# Revit family: Domotics-DomoticSolutions-GEWISS-BUS-KNX_TEMPERATURE_SENSOR
name_source: partatom
category: Apparecchi elettrici
revit_build: Autodesk Revit 2016 (Build: 20161004_0715(x64)
units: mm (PartAtom-declared; Revit-internal decimal feet)

## family parameters
Condiviso = No
Host = Superficie
Mantenere orientamento annotazione = Sì
Punto di calcolo locali = No
Quota connettore circolare = Usa diametro
Taglio con vuoti quando caricato = Sì
Tipo di parte = Normale

## types (18) — shared parameters
Catalogue = DOMOTICS
Catalogue Range = H&B AUTOMATION
IDF = 93389465-b77d-4902-bf96-7a1d22c4ea34
IDT = eb8a331f-fb03-4651-b93d-be283b5d4bed
Immagine tipo = GW14900.jpg
Larghezza sonda = 23 mm  [stored 0.0754593 ft]
No. Chorus modules = 1
No. Chorus modules: = 1
Produttore = GEWISS S.p.A.
Prospetto di default = 1219 mm
SEO = Sensor
Simbolo = SIMBOLO TERMOSTATO : KNX
Technical sheet = https://www.gewiss.com
Tipo = BUS KNX SONDE TERMOREGOLAZIONE_BASE : GW14900 - Titanio
URL = https://www.gewiss.com
Version file RFA = 18.0

## per-type parameters (varying)
| type | Colour | Descrizione | EAN code | Electrocod | Humidity sensor | Modello | Technology | Type |
| GW12799 - Black | Black | KNX TEMPERATURE SENSOR 1M BLACK | 8011564785021 | 3841 |  | GW12799 | KNX | KNX |
| GW12762H - Black - Easy | Black | KNX/EASY HUM./TEMP.SENSORS BLACK | 8011564821989 | 1434 | Built-in | GW12762H |  | KNX |
| GW10762H - White - Easy | White | KNX/EASY HUM./TEMP.SENSORS WHITE | 8011564821972 | 1434 | Built-in | GW10762H |  | KNX |
| GW12900 - Black | Black | F.M.TEMPERATURE SENSOR BLACK | 8011564821927 | 1434 |  | GW12900 |  |  |
| GW10900 - White | White | F.M.TEMPERATURE SENSOR WHITE | 8011564821910 | 1434 |  | GW10900 |  |  |
| GW12769H - Black | Black | EASY HUMIDITY/TEMPERATURE SENSORS BLACK | 8011564809130 | 3841 | Built-in | GW12769H | KNX Easy | KNX Easy |
| GW10799H - White | White | KNX HUMIDITY/TEMPERATURE SENSORS WHITE | 8011564809123 | 3841 | Built-in | GW10799H | KNX | KNX |
| GW14769 - Titanium - Easy | Titanium | EASY TEMPERATURE SENSOR 1M TITANIUM | 8011564785120 | 0144 |  | GW14769 | KNX Easy | KNX Easy |
| GW12799H - Black | Black | KNX HUMIDITY/TEMPERATURE SENSORS BLACK | 8011564809147 | 3841 | Built-in | GW12799H | KNX | KNX |
| GW10799 - White | White | KNX TEMPERATURE SENSOR 1M WHITE | 8011564785014 | 3841 |  | GW10799 | KNX | KNX |
| GW10769 - White - Easy | White | EASY TEMPERATURE SENSOR 1M WHITE | 8011564785106 | 1434 |  | GW10769 | KNX Easy | KNX Easy |
| GW14900 - Titanium | Titanium | F.M.TEMPERATURE SENSOR TITANIUM | 8011564821934 | 1434 |  | GW14900 |  |  |
| GW10769H - White - Easy | White | EASY HUMIDITY/TEMPERATURE SENSORS WHITE | 8011564809116 | 3841 | Built-in | GW10769H | KNX Easy | KNX Easy |
| GW14762H - Titanium - Easy | Titanium | KNX/EASY HUM./TEMP.SENSORS TITANIUM | 8011564821996 | 1434 | Built-in | GW14762H |  | KNX |
| GW14799H - Titanium | Titanium | KNX HUMIDITY/TEMPERATURE SENSORS TIT. | 8011564809161 | 3841 | Built-in | GW14799H | KNX | KNX |
| GW14799 - Titanium | Titanium | KNX TEMPERATURE SENSOR 1M TITANIUM | 8011564785038 | 3841 |  | GW14799 | KNX | KNX |
| GW12769 - Black - Easy | Black | EASY TEMPERATURE SENSOR 1M BLACK | 8011564785113 | 0144 |  | GW12769 | KNX Easy | KNX Easy |
| GW14769H - Titanium - Easy | Titanium | EASY HUMIDITY/TEMPERATURE SENSORS TIT. | 8011564809154 | 3841 | Built-in | GW14769H | KNX Easy | KNX Easy |

note: [stored X ft] marks values corroborated as IEEE doubles in the binary element streams (Revit-internal decimal feet)

## geometry (parser evidence)
native form markers: Blend x2, Sweep x1
no freeform markers — native parametric forms only
